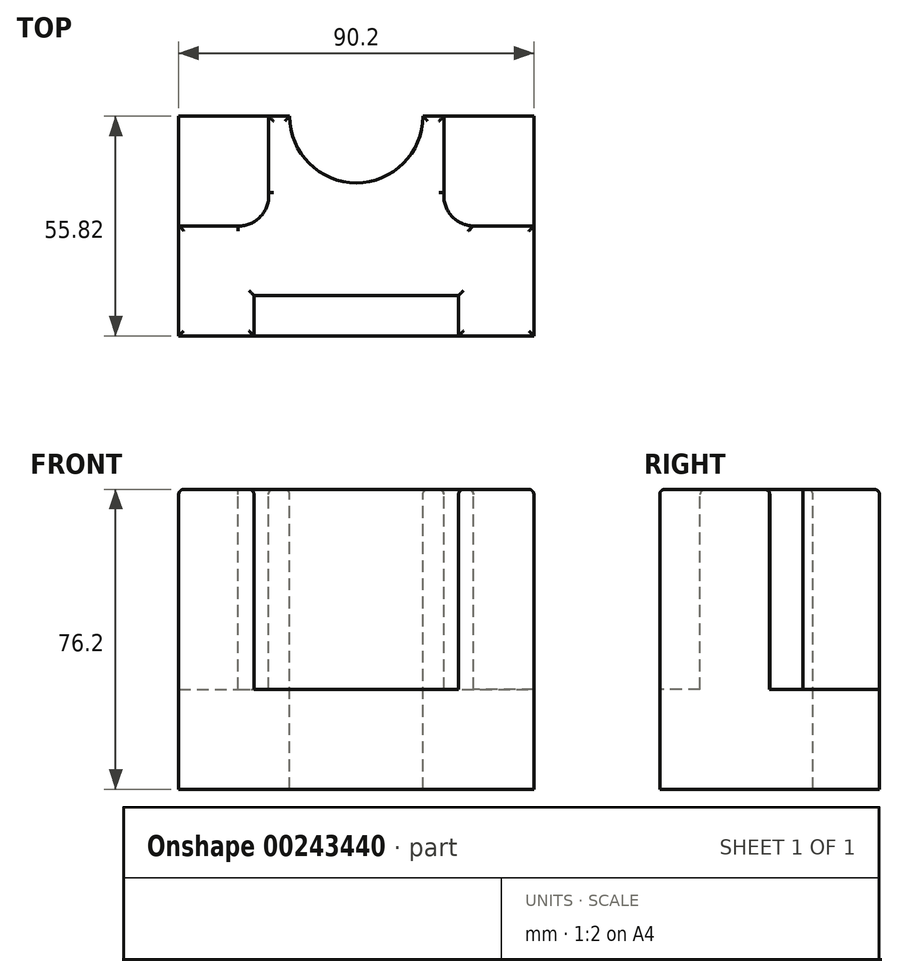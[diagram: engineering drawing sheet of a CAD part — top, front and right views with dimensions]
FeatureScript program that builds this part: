
annotation { "Feature Type Name" : "Feature", "Feature Type Description" : "" }
export const myFeature = defineFeature(function(context is Context, id is Id, definition is map)
    precondition{}
    {
        {
            var Q0;
            Q0=qCreatedBy(makeId("Top.planeOp"),FACE);
            var sketch = newSketch(context, id + "F0", { "sketchPlane" : qUnion([Q0])});
            skLineSegment(sketch, "E0.bottom", {"start": v(-45.1, 27.91) * mm, "end": v(45.1, 27.91) * mm});
            skLineSegment(sketch, "E0.top", {"start": v(-45.1, -27.91) * mm, "end": v(45.1, -27.91) * mm});
            skLineSegment(sketch, "E0.left", {"start": v(-45.1, 27.91) * mm, "end": v(-45.1, -27.91) * mm});
            skLineSegment(sketch, "E0.right", {"start": v(45.1, 27.91) * mm, "end": v(45.1, -27.91) * mm});
            skPoint(sketch, "E0.middle", {"position": v(0, 0) * mm});
            skSolve(sketch);
        }
        {
            var Q0;
            Q0=makeQuery(id+"F0.imprint","IMPRINT",FACE,{"disambiguationData":[TD([[makeQuery(id+"F0.imprint","IMPRINT",EDGE,{"derivedFrom":sQuery(id+"F0.wireOp",EDGE,"E0.bottom")}),-1.0]])]});
            extrude(context, id + "F1", {"entities" : qUnion([Q0]), "depth" : 76.2 * mm});
        }
        {
            var Q0;
            Q0=makeQuery(id+"F1.opExtrude","CAP_FACE",FACE,{"disambiguationData":[OSD([sQuery(id+"F0.wireOp",EDGE,"E0.bottom"),sQuery(id+"F0.wireOp",EDGE,"E0.top"),sQuery(id+"F0.wireOp",EDGE,"E0.left"),sQuery(id+"F0.wireOp",EDGE,"E0.right")])],"isStart":false});
            var sketch = newSketch(context, id + "F2", { "sketchPlane" : qUnion([Q0])});
            skCircle(sketch, "E1", {"center": v(0, 27.91) * mm, "radius": 16.93 * mm});
            skSolve(sketch);
        }
        {
            var Q0;
            Q0 = qSketchRegion(id + "F2", true);
            extrude(context, id + "F3", {"entities" : qUnion([Q0]), "operationType" : NewBodyOperationType.REMOVE, "oppositeDirection" : true, "depth" : 76.2 * mm});
        }
        {
            var Q0;
            Q0=makeQuery(id+"F1.opExtrude","CAP_FACE",FACE,{"disambiguationData":[OSD([sQuery(id+"F0.wireOp",EDGE,"E0.bottom"),sQuery(id+"F0.wireOp",EDGE,"E0.top"),sQuery(id+"F0.wireOp",EDGE,"E0.left"),sQuery(id+"F0.wireOp",EDGE,"E0.right")])],"isStart":false});
            var sketch = newSketch(context, id + "F4", { "sketchPlane" : qUnion([Q0])});
            skLineSegment(sketch, "E2.bottom", {"start": v(26, -17.65) * mm, "end": v(-26, -17.65) * mm});
            skLineSegment(sketch, "E2.top", {"start": v(26, -38.17) * mm, "end": v(-26, -38.17) * mm});
            skLineSegment(sketch, "E2.left", {"start": v(26, -17.65) * mm, "end": v(26, -38.17) * mm});
            skLineSegment(sketch, "E2.right", {"start": v(-26, -17.65) * mm, "end": v(-26, -38.17) * mm});
            skPoint(sketch, "E2.middle", {"position": v(0, -27.91) * mm});
            skSolve(sketch);
        }
        {
            var Q0;
            {var subQ0=sQuery(id+"F4.wireOp",EDGE,"E2.bottom");Q0=makeQuery(id+"F4.imprint","IMPRINT",FACE,{"disambiguationData":[TD([[makeQuery(id+"F4.imprint","IMPRINT",EDGE,{"derivedFrom":subQ0}),1.0]])]});}
            extrude(context, id + "F5", {"entities" : qUnion([Q0]), "operationType" : NewBodyOperationType.REMOVE, "oppositeDirection" : true, "depth" : 50.8 * mm});
        }
        {
            var Q0;
            Q0=makeQuery(id+"F1.opExtrude","CAP_FACE",FACE,{"disambiguationData":[OSD([sQuery(id+"F0.wireOp",EDGE,"E0.bottom"),sQuery(id+"F0.wireOp",EDGE,"E0.top"),sQuery(id+"F0.wireOp",EDGE,"E0.left"),sQuery(id+"F0.wireOp",EDGE,"E0.right")])],"isStart":false});
            var sketch = newSketch(context, id + "F6", { "sketchPlane" : qUnion([Q0])});
            skCircle(sketch, "E3", {"center": v(-29.86, 7.65) * mm, "radius": 7.62 * mm});
            skCircle(sketch, "E4", {"center": v(29.86, 7.65) * mm, "radius": 7.62 * mm});
            skSolve(sketch);
        }
        {
            var Q0;
            Q0=makeQuery(id+"F6.imprint","IMPRINT",FACE,{"disambiguationData":[TD([[makeQuery(id+"F6.imprint","IMPRINT",EDGE,{"derivedFrom":sQuery(id+"F6.wireOp",EDGE,"E3")}),1.0]])]});
            var Q1;
            Q1=makeQuery(id+"F6.imprint","IMPRINT",FACE,{"disambiguationData":[TD([[makeQuery(id+"F6.imprint","IMPRINT",EDGE,{"derivedFrom":sQuery(id+"F6.wireOp",EDGE,"E4")}),1.0]])]});
            extrude(context, id + "F7", {"entities" : qUnion([Q0, Q1]), "operationType" : NewBodyOperationType.REMOVE, "oppositeDirection" : true, "depth" : 50.8 * mm});
        }
        {
            var Q0;
            Q0=makeQuery(id+"F1.opExtrude","CAP_FACE",FACE,{"disambiguationData":[OSD([sQuery(id+"F0.wireOp",EDGE,"E0.bottom"),sQuery(id+"F0.wireOp",EDGE,"E0.top"),sQuery(id+"F0.wireOp",EDGE,"E0.left"),sQuery(id+"F0.wireOp",EDGE,"E0.right")])],"isStart":false});
            var sketch = newSketch(context, id + "F8", { "sketchPlane" : qUnion([Q0])});
            skLineSegment(sketch, "E5.bottom", {"start": v(-45.1, 27.91) * mm, "end": v(-22.28, 27.91) * mm});
            skLineSegment(sketch, "E5.top", {"start": v(-45.1, 6.87) * mm, "end": v(-22.28, 6.87) * mm});
            skLineSegment(sketch, "E5.left", {"start": v(-45.1, 27.91) * mm, "end": v(-45.1, 6.87) * mm});
            skLineSegment(sketch, "E5.right", {"start": v(-22.28, 27.91) * mm, "end": v(-22.28, 6.87) * mm});
            skLineSegment(sketch, "E6.bottom", {"start": v(-45.1, 6.87) * mm, "end": v(-30.01, 6.87) * mm});
            skLineSegment(sketch, "E6.top", {"start": v(-45.1, 0.03) * mm, "end": v(-30.01, 0.03) * mm});
            skLineSegment(sketch, "E6.left", {"start": v(-45.1, 6.87) * mm, "end": v(-45.1, 0.03) * mm});
            skLineSegment(sketch, "E6.right", {"start": v(-30.01, 6.87) * mm, "end": v(-30.01, 0.03) * mm});
            skLineSegment(sketch, "E7.bottom", {"start": v(45.1, 27.91) * mm, "end": v(22.28, 27.91) * mm});
            skLineSegment(sketch, "E7.top", {"start": v(45.1, 6.87) * mm, "end": v(22.28, 6.87) * mm});
            skLineSegment(sketch, "E7.left", {"start": v(45.1, 27.91) * mm, "end": v(45.1, 6.87) * mm});
            skLineSegment(sketch, "E7.right", {"start": v(22.28, 27.91) * mm, "end": v(22.28, 6.87) * mm});
            skLineSegment(sketch, "E8.bottom", {"start": v(45.1, 6.87) * mm, "end": v(29.74, 6.87) * mm});
            skLineSegment(sketch, "E8.top", {"start": v(45.1, 0) * mm, "end": v(29.74, 0) * mm});
            skLineSegment(sketch, "E8.left", {"start": v(45.1, 6.87) * mm, "end": v(45.1, 0) * mm});
            skLineSegment(sketch, "E8.right", {"start": v(29.74, 6.87) * mm, "end": v(29.74, 0) * mm});
            skLineSegment(sketch, "E9.bottom", {"start": v(-45.1, 0.03) * mm, "end": v(-35.55, 0.03) * mm});
            skLineSegment(sketch, "E9.top", {"start": v(-45.1, -27.91) * mm, "end": v(-35.55, -27.91) * mm});
            skLineSegment(sketch, "E9.left", {"start": v(-45.1, 0.03) * mm, "end": v(-45.1, -27.91) * mm});
            skLineSegment(sketch, "E9.right", {"start": v(-35.55, 0.03) * mm, "end": v(-35.55, -27.91) * mm});
            skLineSegment(sketch, "E10.bottom", {"start": v(45.1, 0) * mm, "end": v(35.55, 0) * mm});
            skLineSegment(sketch, "E10.top", {"start": v(45.1, -27.91) * mm, "end": v(35.55, -27.91) * mm});
            skLineSegment(sketch, "E10.left", {"start": v(45.1, 0) * mm, "end": v(45.1, -27.91) * mm});
            skLineSegment(sketch, "E10.right", {"start": v(35.55, 0) * mm, "end": v(35.55, -27.91) * mm});
            skSolve(sketch);
        }
        {
            var Q0;
            {var subQ5=sQuery(id+"F8.wireOp",EDGE,"E5.bottom");Q0=makeQuery(id+"F8.imprint","IMPRINT",FACE,{"disambiguationData":[TD([[makeQuery(id+"F8.imprint","IMPRINT",EDGE,{"derivedFrom":subQ5}),-1.0]])]});}
            var Q1;
            {var subQ1=sQuery(id+"F8.wireOp",EDGE,"E6.top");Q1=makeQuery(id+"F8.imprint","IMPRINT",FACE,{"disambiguationData":[TD([[makeQuery(id+"F8.imprint","IMPRINT",EDGE,{"derivedFrom":subQ1}),1.0]])]});}
            var Q2;
            Q2=makeQuery(id+"F8.imprint","IMPRINT",FACE,{"disambiguationData":[TD([[makeQuery(id+"F8.imprint","IMPRINT",EDGE,{"derivedFrom":sQuery(id+"F8.wireOp",EDGE,"E9.bottom")}),-1.0]])]});
            var Q3;
            {var subQ5=sQuery(id+"F8.wireOp",EDGE,"E7.bottom");Q3=makeQuery(id+"F8.imprint","IMPRINT",FACE,{"disambiguationData":[TD([[makeQuery(id+"F8.imprint","IMPRINT",EDGE,{"derivedFrom":subQ5}),-1.0]])]});}
            var Q4;
            {var subQ1=sQuery(id+"F8.wireOp",EDGE,"E8.top");Q4=makeQuery(id+"F8.imprint","IMPRINT",FACE,{"disambiguationData":[TD([[makeQuery(id+"F8.imprint","IMPRINT",EDGE,{"derivedFrom":subQ1}),-1.0]])]});}
            var Q5;
            Q5=makeQuery(id+"F8.imprint","IMPRINT",FACE,{"disambiguationData":[TD([[makeQuery(id+"F8.imprint","IMPRINT",EDGE,{"derivedFrom":sQuery(id+"F8.wireOp",EDGE,"E10.bottom")}),1.0]])]});
            extrude(context, id + "F9", {"entities" : qUnion([Q0, Q1, Q2, Q3, Q4, Q5]), "operationType" : NewBodyOperationType.REMOVE, "oppositeDirection" : true, "depth" : 50.8 * mm});
        }
        {
            var Q0;
            Q0=makeQuery(id+"F9.boolean.opBoolean","COPY",EDGE,{"derivedFrom":makeQuery(id+"F9.opExtrude","CAP_EDGE",EDGE,{"disambiguationData":[OSD([sQuery(id+"F8.wireOp",EDGE,"E5.bottom")])],"isStart":false})});
            var Q1;
            Q1=makeQuery(id+"F9.boolean.opBoolean","COPY",EDGE,{"derivedFrom":makeQuery(id+"F9.opExtrude","CAP_EDGE",EDGE,{"disambiguationData":[OSD([sQuery(id+"F8.wireOp",EDGE,"E7.bottom")])],"isStart":false})});
            var Q2;
            {var subQ0=sQuery(id+"F0.wireOp",EDGE,"E0.bottom");var subQ1=sQuery(id+"F0.wireOp",EDGE,"E0.right");Q2=makeQuery(id+"F3.boolean.opBoolean","SPLIT",EDGE,{"disambiguationData":[TD([makeQuery(id+"F1.opExtrude","SWEPT_FACE",FACE,{"disambiguationData":[OSD([subQ1])]})])],"derivedFrom":makeQuery(id+"F1.opExtrude","CAP_EDGE",EDGE,{"disambiguationData":[OSD([subQ0])],"isStart":false})});}
            var Q3;
            {var subQ0=sQuery(id+"F0.wireOp",EDGE,"E0.bottom");var subQ1=sQuery(id+"F0.wireOp",EDGE,"E0.left");Q3=makeQuery(id+"F3.boolean.opBoolean","SPLIT",EDGE,{"disambiguationData":[TD([makeQuery(id+"F1.opExtrude","SWEPT_FACE",FACE,{"disambiguationData":[OSD([subQ1])]})])],"derivedFrom":makeQuery(id+"F1.opExtrude","CAP_EDGE",EDGE,{"disambiguationData":[OSD([subQ0])],"isStart":false})});}
            var Q4;
            Q4=makeQuery(id+"F3.boolean.opBoolean","COPY",EDGE,{"derivedFrom":makeQuery(id+"F3.opExtrude","CAP_EDGE",EDGE,{"disambiguationData":[OSD([sQuery(id+"F2.wireOp",EDGE,"E1")])],"isStart":true})});
            var Q5;
            Q5=makeQuery(id+"F1.opExtrude","CAP_FACE",FACE,{"disambiguationData":[OSD([sQuery(id+"F0.wireOp",EDGE,"E0.bottom"),sQuery(id+"F0.wireOp",EDGE,"E0.top"),sQuery(id+"F0.wireOp",EDGE,"E0.left"),sQuery(id+"F0.wireOp",EDGE,"E0.right")])],"isStart":false});
            var Q6;
            Q6=makeQuery(id+"F5.boolean.opBoolean","COPY",EDGE,{"derivedFrom":makeQuery(id+"F5.opExtrude","CAP_EDGE",EDGE,{"disambiguationData":[OSD([sQuery(id+"F0.wireOp",EDGE,"E0.top")])],"isStart":false})});
            var Q7;
            Q7=makeQuery(id+"F9.boolean.opBoolean","COPY",EDGE,{"derivedFrom":makeQuery(id+"F9.opExtrude","CAP_EDGE",EDGE,{"disambiguationData":[OSD([sQuery(id+"F8.wireOp",EDGE,"E9.top")])],"isStart":false})});
            var Q8;
            Q8=makeQuery(id+"F9.boolean.opBoolean","COPY",EDGE,{"derivedFrom":makeQuery(id+"F9.opExtrude","CAP_EDGE",EDGE,{"disambiguationData":[OSD([sQuery(id+"F8.wireOp",EDGE,"E5.left"),sQuery(id+"F8.wireOp",EDGE,"E6.left"),sQuery(id+"F8.wireOp",EDGE,"E9.left")])],"isStart":false})});
            var Q9;
            Q9=makeQuery(id+"F9.boolean.opBoolean","COPY",EDGE,{"derivedFrom":makeQuery(id+"F9.opExtrude","CAP_EDGE",EDGE,{"disambiguationData":[OSD([sQuery(id+"F8.wireOp",EDGE,"E7.left"),sQuery(id+"F8.wireOp",EDGE,"E8.left"),sQuery(id+"F8.wireOp",EDGE,"E10.left")])],"isStart":false})});
            var Q10;
            Q10=makeQuery(id+"F9.boolean.opBoolean","COPY",EDGE,{"derivedFrom":makeQuery(id+"F9.opExtrude","CAP_EDGE",EDGE,{"disambiguationData":[OSD([sQuery(id+"F8.wireOp",EDGE,"E10.top")])],"isStart":false})});
            fillet(context, id + "F10", {"entities" : qUnion([Q0, Q1, Q2, Q3, Q4, Q5, Q6, Q7, Q8, Q9, Q10]), "radius" : 1.27 * mm, "tangentPropagation" : true, "allowEdgeOverflow" : false});
        }
    });
